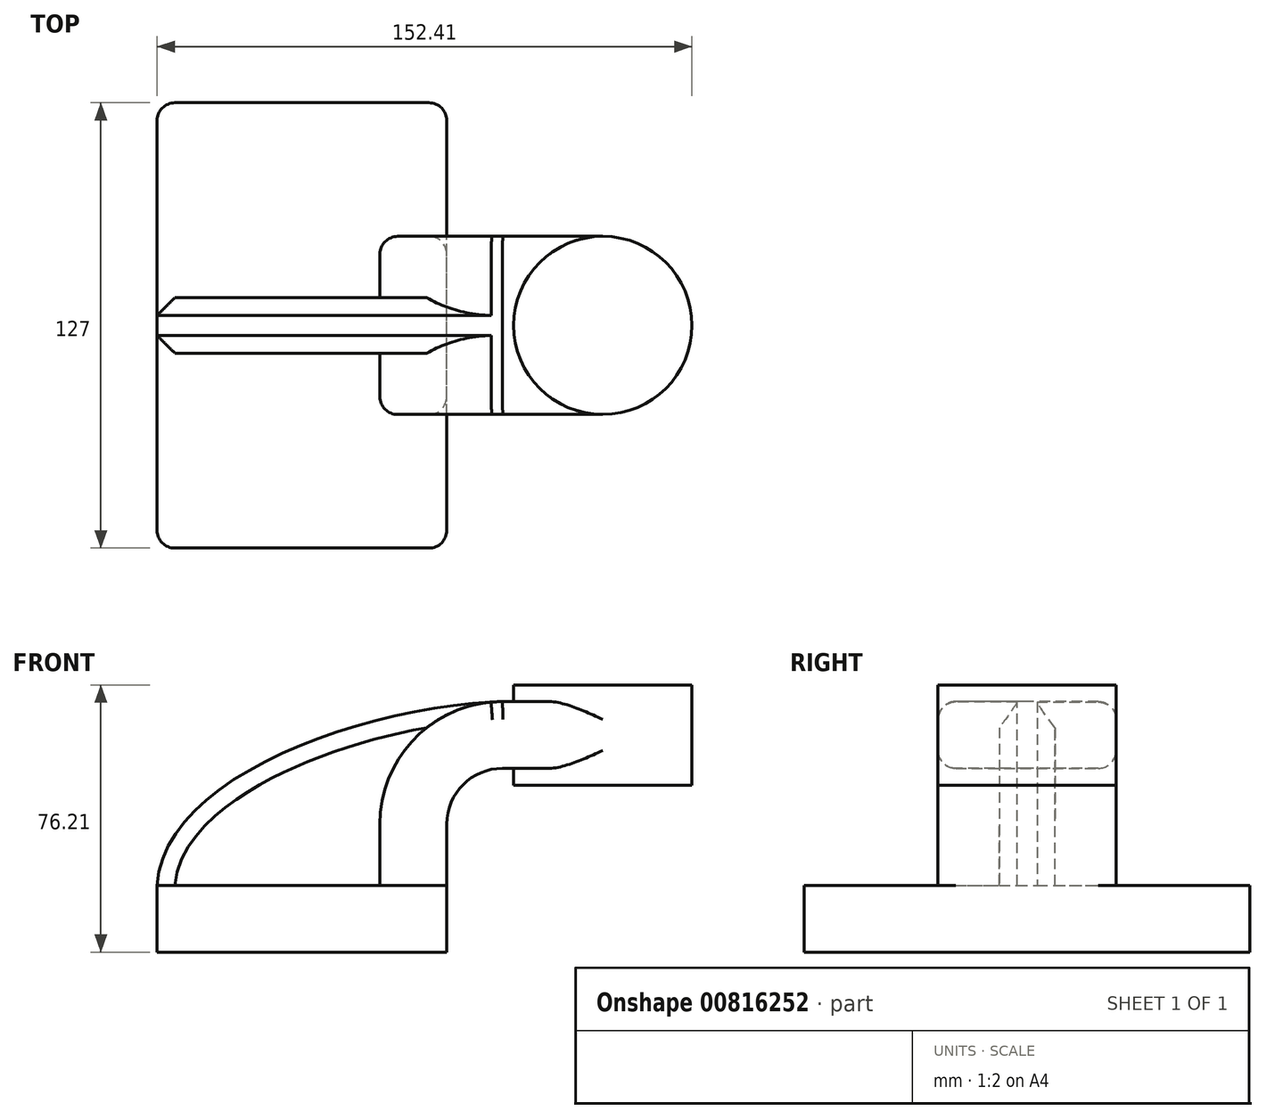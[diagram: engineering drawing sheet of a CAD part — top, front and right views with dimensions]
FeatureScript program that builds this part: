
annotation { "Feature Type Name" : "Feature", "Feature Type Description" : "" }
export const myFeature = defineFeature(function(context is Context, id is Id, definition is map)
    precondition{}
    {
        {
            var Q0;
            Q0=qCreatedBy(makeId("Front.planeOp"),FACE);
            var sketch = newSketch(context, id + "F0", { "sketchPlane" : qUnion([Q0])});
            skLineSegment(sketch, "E0.rect.bottom", {"start": v(-41.28, 9.52) * mm, "end": v(41.28, 9.52) * mm});
            skLineSegment(sketch, "E0.rect.top", {"start": v(-41.28, -9.52) * mm, "end": v(41.28, -9.52) * mm});
            skLineSegment(sketch, "E0.rect.left", {"start": v(-41.28, 9.52) * mm, "end": v(-41.28, -9.52) * mm});
            skLineSegment(sketch, "E0.rect.right", {"start": v(41.28, 9.52) * mm, "end": v(41.28, -9.52) * mm});
            skPoint(sketch, "E0.rect.middle", {"position": v(0, 0) * mm});
            skLineSegment(sketch, "E1", {"start": v(41.28, 9.52) * mm, "end": v(41.28, 27) * mm});
            skArc(sketch, "E2", {"start": v(41.28, 27) * mm, "mid": v(45.92, 38.23) * mm, "end": v(57.15, 42.88) * mm});
            skLineSegment(sketch, "E3", {"start": v(57.15, 42.88) * mm, "end": v(85.72, 42.88) * mm});
            skLineSegment(sketch, "E4.rect.bottom", {"start": v(60.32, 38.1) * mm, "end": v(111.12, 38.1) * mm});
            skLineSegment(sketch, "E4.rect.top", {"start": v(60.32, 66.68) * mm, "end": v(111.12, 66.68) * mm});
            skLineSegment(sketch, "E4.rect.left", {"start": v(60.32, 38.1) * mm, "end": v(60.32, 66.68) * mm});
            skLineSegment(sketch, "E4.rect.right", {"start": v(111.13, 38.1) * mm, "end": v(111.12, 66.68) * mm});
            skPoint(sketch, "E4.rect.middle", {"position": v(85.72, 52.39) * mm});
            skLineSegment(sketch, "E5.0", {"start": v(57.15, 61.93) * mm, "end": v(85.72, 61.93) * mm});
            skArc(sketch, "E5.1", {"start": v(22.23, 27) * mm, "mid": v(32.45, 51.7) * mm, "end": v(57.15, 61.93) * mm});
            skLineSegment(sketch, "E5.2", {"start": v(22.23, 9.52) * mm, "end": v(22.23, 27) * mm});
            skLineSegment(sketch, "E6", {"start": v(85.72, 38.1) * mm, "end": v(85.72, 66.68) * mm});
            skFitSpline(sketch, "E7", {"points": [v(-41.28, 9.53) * mm, v(57.15, 61.93) * mm], "startDerivative": vector(5.2, 92.34) * mm, "endDerivative": vector(120.92, 4.22) * mm});
            skSolve(sketch);
        }
        {
            var Q0;
            Q0=makeQuery(id+"F0.imprint","IMPRINT",FACE,{"disambiguationData":[TD([[makeQuery(id+"F0.imprint","IMPRINT",EDGE,{"derivedFrom":sQuery(id+"F0.wireOp",EDGE,"E0.rect.top")}),1.0]])]});
            extrude(context, id + "F1", {"entities" : qUnion([Q0]), "endBound" : BoundingType.SYMMETRIC, "depth" : 127 * mm});
        }
        {
            var Q0;
            {var subQ9=sQuery(id+"F0.wireOp",EDGE,"E1");Q0=makeQuery(id+"F0.imprint","IMPRINT",FACE,{"disambiguationData":[TD([[makeQuery(id+"F0.imprint","IMPRINT",EDGE,{"derivedFrom":subQ9}),1.0]])]});}
            var Q1;
            {var subQ0=sQuery(id+"F0.wireOp",EDGE,"E6");var subQ1=sQuery(id+"F0.wireOp",EDGE,"E3");var subQ2=makeQuery(id+"F0.imprint","INTERSECT",VERTEX,{"derivedFrom":[subQ1,subQ0]});Q1=makeQuery(id+"F0.imprint","IMPRINT",FACE,{"disambiguationData":[TD([[makeQuery(id+"F0.imprint","IMPRINT",EDGE,{"disambiguationData":[TD([[subQ2,1.0]])],"derivedFrom":subQ1}),1.0]])]});}
            extrude(context, id + "F2", {"entities" : qUnion([Q0, Q1]), "operationType" : NewBodyOperationType.ADD, "endBound" : BoundingType.SYMMETRIC, "depth" : 50.8 * mm});
        }
        {
            var Q0;
            {var subQ3=sQuery(id+"F0.wireOp",EDGE,"E5.2");Q0=makeQuery(id+"F0.imprint","IMPRINT",FACE,{"disambiguationData":[TD([[makeQuery(id+"F0.imprint","IMPRINT",EDGE,{"derivedFrom":subQ3}),1.0]])]});}
            extrude(context, id + "F3", {"entities" : qUnion([Q0]), "operationType" : NewBodyOperationType.ADD, "endBound" : BoundingType.SYMMETRIC, "depth" : 15.88 * mm});
        }
        {
            var Q0;
            {var subQ5=sQuery(id+"F0.wireOp",EDGE,"E4.rect.right");Q0=makeQuery(id+"F0.imprint","IMPRINT",FACE,{"disambiguationData":[TD([[makeQuery(id+"F0.imprint","IMPRINT",EDGE,{"derivedFrom":subQ5}),1.0]])]});}
            var Q1;
            Q1=sQuery(id+"F0.wireOp",EDGE,"E6");
            revolve(context, id + "F4", {"operationType" : NewBodyOperationType.ADD, "entities" : qUnion([Q0]), "axis" : qUnion([Q1]), "revolveType" : RevolveType.FULL});
        }
        {
            var Q0;
            Q0=makeQuery(id+"F1.opExtrude","CAP_EDGE",EDGE,{"disambiguationData":[OSD([sQuery(id+"F0.wireOp",EDGE,"E0.rect.right")])],"isStart":false});
            var Q1;
            Q1=makeQuery(id+"F1.opExtrude","CAP_EDGE",EDGE,{"disambiguationData":[OSD([sQuery(id+"F0.wireOp",EDGE,"E0.rect.left")])],"isStart":false});
            var Q2;
            Q2=makeQuery(id+"F1.opExtrude","CAP_EDGE",EDGE,{"disambiguationData":[OSD([sQuery(id+"F0.wireOp",EDGE,"E0.rect.right")])],"isStart":true});
            var Q3;
            Q3=makeQuery(id+"F1.opExtrude","CAP_EDGE",EDGE,{"disambiguationData":[OSD([sQuery(id+"F0.wireOp",EDGE,"E0.rect.left")])],"isStart":true});
            fillet(context, id + "F5", {"entities" : qUnion([Q0, Q1, Q2, Q3]), "radius" : 5.08 * mm, "tangentPropagation" : true, "allowEdgeOverflow" : false});
        }
        {
            var Q0;
            Q0=makeQuery(id+"F2.opExtrude","CAP_EDGE",EDGE,{"disambiguationData":[OSD([sQuery(id+"F0.wireOp",EDGE,"E5.0")])],"isStart":false});
            var Q1;
            Q1=makeQuery(id+"F2.opExtrude","CAP_EDGE",EDGE,{"disambiguationData":[OSD([sQuery(id+"F0.wireOp",EDGE,"E3")])],"isStart":false});
            var Q2;
            Q2=makeQuery(id+"F2.opExtrude","CAP_EDGE",EDGE,{"disambiguationData":[OSD([sQuery(id+"F0.wireOp",EDGE,"E1")])],"isStart":false});
            var Q3;
            Q3=makeQuery(id+"F2.opExtrude","CAP_EDGE",EDGE,{"disambiguationData":[OSD([sQuery(id+"F0.wireOp",EDGE,"E5.2")])],"isStart":false});
            fillet(context, id + "F6", {"entities" : qUnion([Q0, Q1, Q2, Q3]), "radius" : 5.08 * mm, "tangentPropagation" : true, "allowEdgeOverflow" : false});
        }
        {
            var Q0;
            Q0=makeQuery(id+"F2.opExtrude","CAP_EDGE",EDGE,{"disambiguationData":[OSD([sQuery(id+"F0.wireOp",EDGE,"E5.0")])],"isStart":true});
            var Q1;
            Q1=makeQuery(id+"F2.opExtrude","CAP_EDGE",EDGE,{"disambiguationData":[OSD([sQuery(id+"F0.wireOp",EDGE,"E5.2")])],"isStart":true});
            var Q2;
            Q2=makeQuery(id+"F2.opExtrude","CAP_EDGE",EDGE,{"disambiguationData":[OSD([sQuery(id+"F0.wireOp",EDGE,"E1")])],"isStart":true});
            var Q3;
            Q3=makeQuery(id+"F2.opExtrude","CAP_EDGE",EDGE,{"disambiguationData":[OSD([sQuery(id+"F0.wireOp",EDGE,"E3")])],"isStart":true});
            fillet(context, id + "F7", {"entities" : qUnion([Q0, Q1, Q2, Q3]), "radius" : 5.08 * mm, "tangentPropagation" : true, "allowEdgeOverflow" : false});
        }
        {
            var Q0;
            Q0=makeQuery(id+"F3.opExtrude","CAP_EDGE",EDGE,{"disambiguationData":[OSD([sQuery(id+"F0.wireOp",EDGE,"E7")])],"isStart":true});
            var Q1;
            Q1=makeQuery(id+"F3.opExtrude","CAP_EDGE",EDGE,{"disambiguationData":[OSD([sQuery(id+"F0.wireOp",EDGE,"E7")])],"isStart":false});
            chamfer(context, id + "F8", {"entities" : qUnion([Q0, Q1]), "width" : 5.08 * mm, "tangentPropagation" : true});
        }
    });
